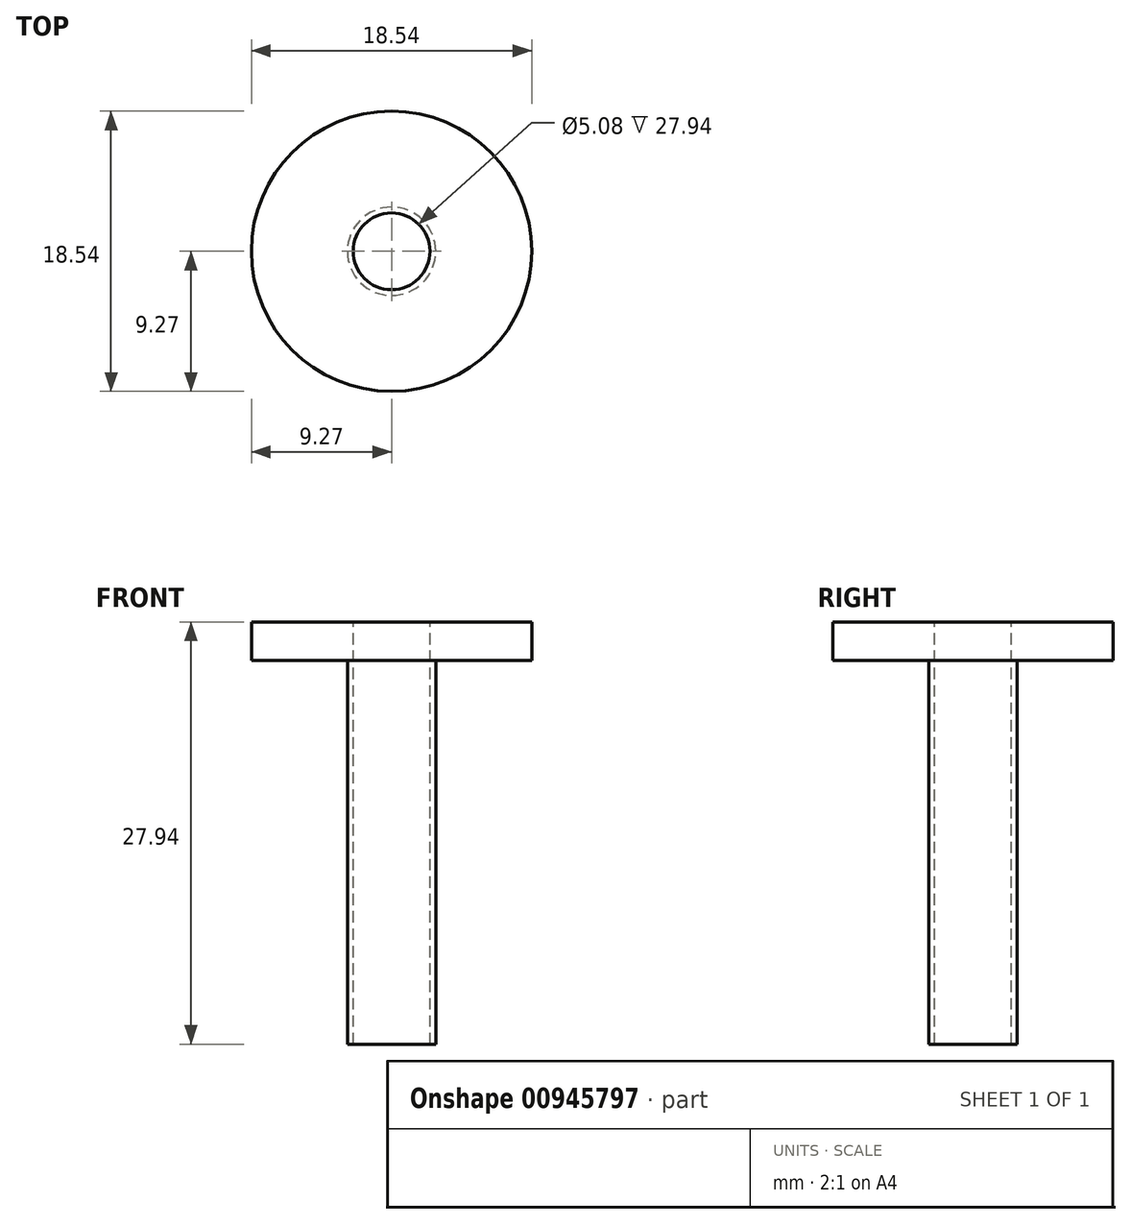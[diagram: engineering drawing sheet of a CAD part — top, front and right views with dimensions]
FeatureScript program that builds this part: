
annotation { "Feature Type Name" : "Feature", "Feature Type Description" : "" }
export const myFeature = defineFeature(function(context is Context, id is Id, definition is map)
    precondition{}
    {
        {
            var Q0;
            Q0=qCreatedBy(makeId("Front.planeOp"),FACE);
            var sketch = newSketch(context, id + "F0", { "sketchPlane" : qUnion([Q0])});
            skLineSegment(sketch, "E0", {"start": v(-50.97, 30.63) * mm, "end": v(-50.97, 5.23) * mm});
            skLineSegment(sketch, "E1", {"start": v(-50.97, 30.63) * mm, "end": v(-44.62, 30.63) * mm});
            skLineSegment(sketch, "E2", {"start": v(-44.62, 30.63) * mm, "end": v(-44.62, 33.17) * mm});
            skLineSegment(sketch, "E3", {"start": v(-50.97, 5.23) * mm, "end": v(-53.9, 5.23) * mm});
            skLineSegment(sketch, "E4", {"start": v(-53.9, 33.17) * mm, "end": v(-44.62, 33.17) * mm});
            skLineSegment(sketch, "E5", {"start": v(-53.9, 33.17) * mm, "end": v(-53.9, 5.23) * mm});
            skSolve(sketch);
        }
        {
            var Q0;
            Q0 = qSketchRegion(id + "F0", true);
            var Q1;
            Q1=sQuery(id+"F0.wireOp",EDGE,"E5");
            var Q2;
            Q2=sQuery(id+"F0.wireOp",EDGE,"E5");
            revolve(context, id + "F1", {"surfaceOperationType" : NewSurfaceOperationType.NEW, "entities" : qUnion([Q0]), "surfaceEntities" : qUnion([Q1]), "axis" : qUnion([Q2]), "revolveType" : RevolveType.FULL});
        }
        {
            var Q0;
            Q0=makeQuery(id+"F1.opRevolve","SWEPT_FACE",FACE,{"disambiguationData":[OSD([sQuery(id+"F0.wireOp",EDGE,"E4")])]});
            var sketch = newSketch(context, id + "F2", { "sketchPlane" : qUnion([Q0])});
            skCircle(sketch, "E6", {"center": v(-53.9, 0) * mm, "radius": 2.54 * mm});
            skSolve(sketch);
        }
        {
            var Q0;
            Q0 = qSketchRegion(id + "F2", true);
            extrude(context, id + "F3", {"entities" : qUnion([Q0]), "operationType" : NewBodyOperationType.REMOVE, "oppositeDirection" : true, "depth" : 31.75 * mm, "offsetDistance" : 25.4 * mm});
        }
    });
